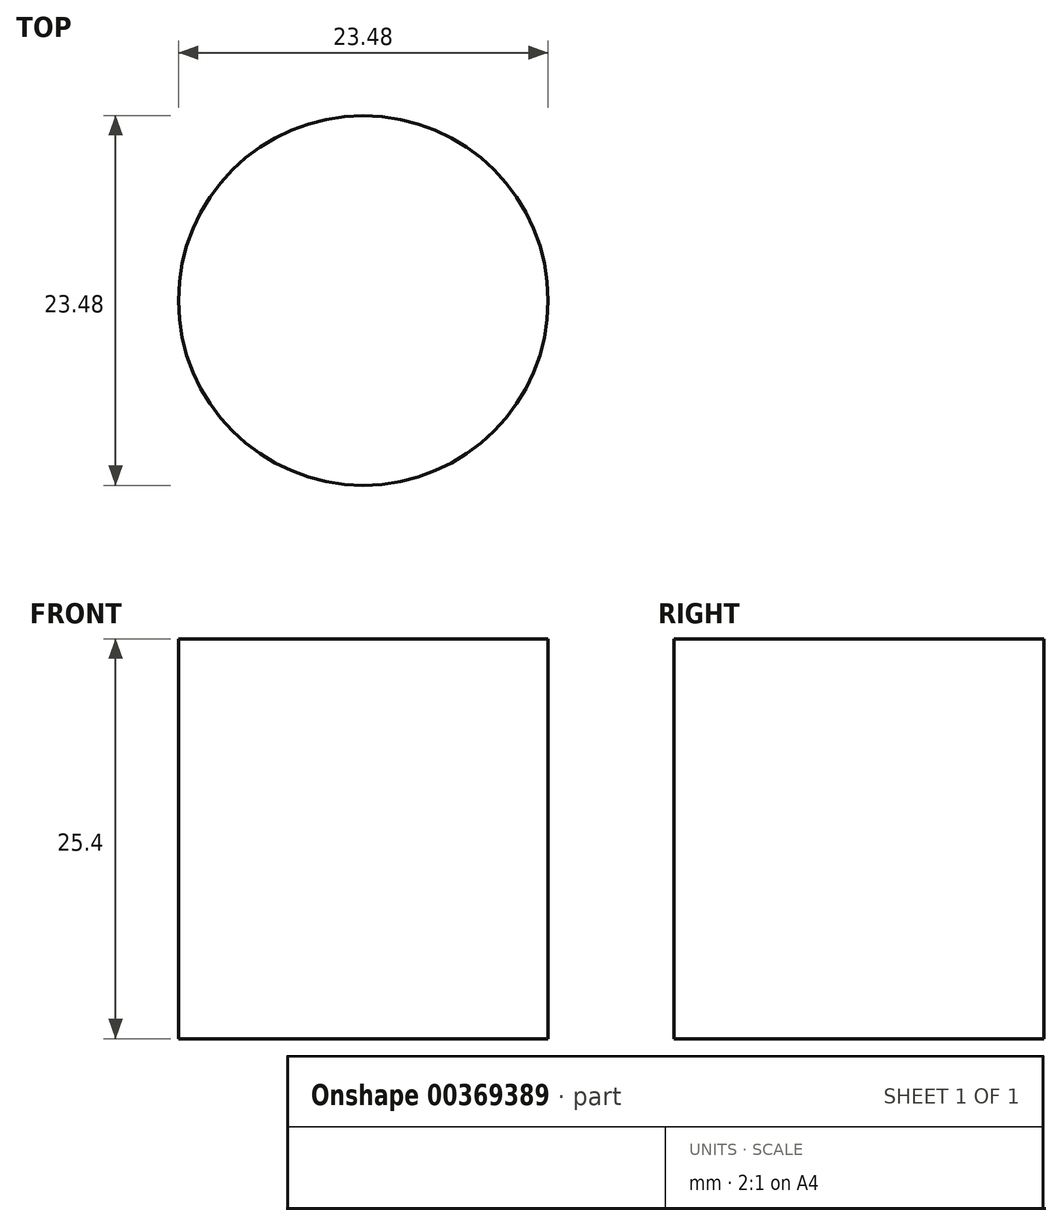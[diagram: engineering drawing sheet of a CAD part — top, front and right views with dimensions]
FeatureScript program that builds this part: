
annotation { "Feature Type Name" : "Feature", "Feature Type Description" : "" }
export const myFeature = defineFeature(function(context is Context, id is Id, definition is map)
    precondition{}
    {
        {
            var Q0;
            Q0=qCreatedBy(makeId("Top.planeOp"),FACE);
            var sketch = newSketch(context, id + "F0", { "sketchPlane" : qUnion([Q0])});
            skCircle(sketch, "E0", {"center": v(0, 0) * mm, "radius": 27.98 * mm});
            skCircle(sketch, "E1", {"center": v(0, 0) * mm, "radius": 11.74 * mm});
            skSolve(sketch);
        }
        {
            var Q0;
            Q0=makeQuery(id+"F0.imprint","IMPRINT",FACE,{"disambiguationData":[TD([[makeQuery(id+"F0.imprint","IMPRINT",EDGE,{"derivedFrom":sQuery(id+"F0.wireOp",EDGE,"E1")}),1.0]])]});
            extrude(context, id + "F1", {"entities" : qUnion([Q0]), "depth" : 25.4 * mm});
        }
    });
